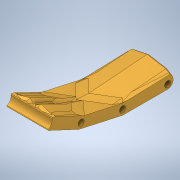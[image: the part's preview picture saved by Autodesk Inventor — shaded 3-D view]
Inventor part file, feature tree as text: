
AUTODESK INVENTOR PART (.ipt)
format: ipt  version: 2020 (Build 240168000, 168)  size: 339,456 bytes
history: native  units: in
note: dims shown in document units (in); Inventor stores cm internally (conversion verified against a paired STEP export)
features: chamfer x12, sketch x7, extrude x6, fillet x3, projected_geometry x1
ambient origin geometry x8: Origin, YZ Plane, XZ Plane, XY Plane, X Axis, Y Axis, Z Axis, Center Point
bodies: Solid1 (feature_tree)
feature tree (29):
  extrude  "Extrusion1"  Depth=1.378in
  extrude  "Extrusion2"  Depth=0.1969in TaperAngle=45.0deg
  chamfer  "Chamfer1"  Distance=0.1969in Angle=45.0deg
  chamfer  "Chamfer2"  Distance=0.1181in Angle=45.0deg
  chamfer  "Chamfer3"  Distance=0.0787in Angle=45.0deg
  chamfer  "Chamfer5"  Distance=1.378in
  extrude  "Extrusion3"  Depth=0.0787in TaperAngle=45.0deg
  chamfer  "Chamfer6"  Distance=0.0394in Angle=45.0deg
  chamfer  "Chamfer8"  Distance=0.0394in Angle=45.0deg
  chamfer  "Chamfer9"  Distance=0.1969in
  chamfer  "Chamfer10"  Distance=0.1969in
  fillet  "Fillet1"  Radius=0.1575in
  fillet  "Fillet2"  Radius=0.1575in
  fillet  "Fillet3"  Radius=0.3937in
  chamfer  "Chamfer11"  Distance=0.0787in Angle=45.0deg
  chamfer  "Chamfer12"  Distance=0.3717in
  extrude  "Extrusion4"  Depth=0.0197in
  chamfer  "Chamfer13"  Distance=0.1102in
  sketch  "Sketch7"  dims[d22=0.1181in d23=1.378in d24=0.0in]
  extrude  "Extrusion5"  Depth=0.3937in TaperAngle=0.0deg
  extrude  "Extrusion6"  Depth=0.0197in
  chamfer  "Chamfer15"  Distance=0.4843in
  sketch  "Sketch1"  dims[d0=1.378in d1=0.0in d2=0.5906in]
  sketch  "Sketch2"  dims[d3=1.378in d4=0.0in d5=0.1969in d6=0.689in d7=45.0deg d8=0.1969in d9=0.689in d10=45.0deg d11=0.1181in d12=0.689in d13=45.0deg d17=0.0787in d18=0.689in d19=45.0deg]
  sketch  "Sketch4"  dims[d20=0.1772in]
  sketch  "Sketch5"  dims[d21=0.1772in]
  projected_geometry  "Projected Loop2"
  sketch  "Sketch8"  dims[d25=0.0787in d26=0.689in d27=45.0deg d31=0.0787in d32=0.689in d33=45.0deg d34=0.0394in d35=0.689in d36=45.0deg d37=0.0394in d38=0.689in d39=45.0deg]
  sketch  "Sketch9"  dims[d40=0.1969in d41=0.1969in d42=0.1969in d43=0.1575in d44=0.689in d45=45.0deg d46=0.1575in d47=0.689in d48=45.0deg d49=0.3937in d50=0.0in d51=0.0787in d52=0.0787in d53=45.0deg d54=0.3717in d55=0.2047in d56=0.1102in d57=0.3937in d58=0.0in d62=0.5648in d63=0.4843in d64=0.1102in d65=0.3937in d66=0.0in d67=0.0197in d68=0.0787in d69=45.0deg]
